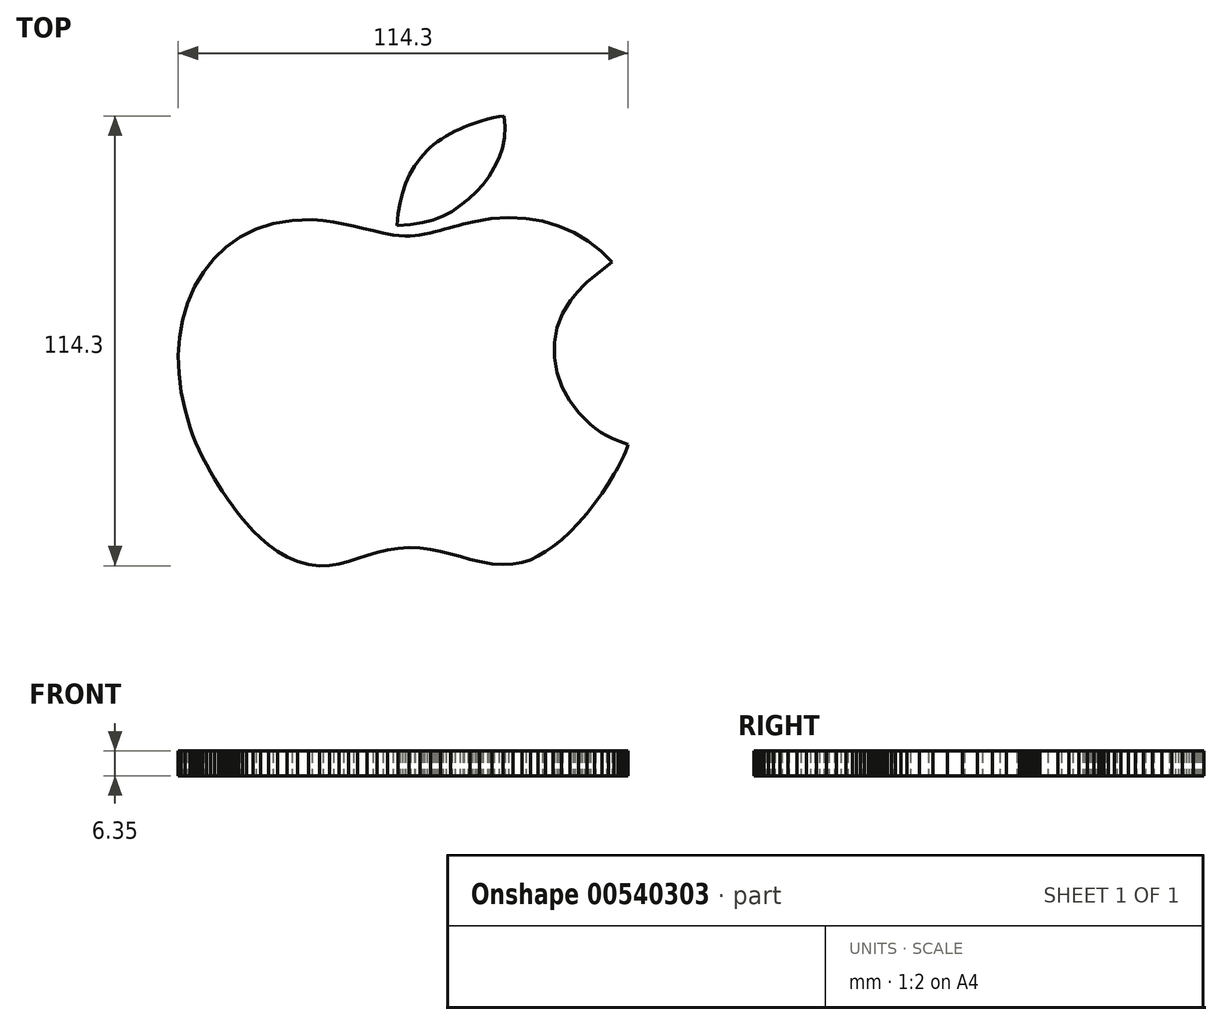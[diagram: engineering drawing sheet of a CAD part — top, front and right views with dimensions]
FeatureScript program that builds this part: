
annotation { "Feature Type Name" : "Feature", "Feature Type Description" : "" }
export const myFeature = defineFeature(function(context is Context, id is Id, definition is map)
    precondition{}
    {
        {
            var Q0;
            Q0=qCreatedBy(makeId("Top.planeOp"),FACE);
            var sketch = newSketch(context, id + "F0", { "sketchPlane" : qUnion([Q0])});
            skLineSegment(sketch, "E0", {"start": v(57.15, -26.3) * mm, "end": v(55.03, -25.53) * mm});
            skLineSegment(sketch, "E1", {"start": v(55.03, -25.53) * mm, "end": v(53.22, -24.8) * mm});
            skLineSegment(sketch, "E2", {"start": v(53.22, -24.8) * mm, "end": v(51.63, -24.04) * mm});
            skLineSegment(sketch, "E3", {"start": v(51.63, -24.04) * mm, "end": v(50.21, -23.21) * mm});
            skLineSegment(sketch, "E4", {"start": v(50.21, -23.21) * mm, "end": v(48.87, -22.28) * mm});
            skLineSegment(sketch, "E5", {"start": v(48.87, -22.28) * mm, "end": v(47.55, -21.17) * mm});
            skLineSegment(sketch, "E6", {"start": v(47.55, -21.17) * mm, "end": v(46.17, -19.86) * mm});
            skLineSegment(sketch, "E7", {"start": v(46.17, -19.86) * mm, "end": v(44.66, -18.29) * mm});
            skLineSegment(sketch, "E8", {"start": v(44.66, -18.29) * mm, "end": v(42.21, -15.16) * mm});
            skLineSegment(sketch, "E9", {"start": v(42.21, -15.16) * mm, "end": v(40.35, -11.72) * mm});
            skLineSegment(sketch, "E10", {"start": v(40.35, -11.72) * mm, "end": v(39.1, -8.04) * mm});
            skLineSegment(sketch, "E11", {"start": v(39.1, -8.04) * mm, "end": v(38.46, -4.24) * mm});
            skLineSegment(sketch, "E12", {"start": v(38.46, -4.24) * mm, "end": v(38.47, -0.4) * mm});
            skLineSegment(sketch, "E13", {"start": v(38.47, -0.4) * mm, "end": v(39.13, 3.35) * mm});
            skLineSegment(sketch, "E14", {"start": v(39.13, 3.35) * mm, "end": v(40.47, 6.94) * mm});
            skLineSegment(sketch, "E15", {"start": v(40.47, 6.94) * mm, "end": v(42.51, 10.25) * mm});
            skLineSegment(sketch, "E16", {"start": v(42.51, 10.25) * mm, "end": v(43.1, 11) * mm});
            skLineSegment(sketch, "E17", {"start": v(43.1, 11) * mm, "end": v(43.69, 11.73) * mm});
            skLineSegment(sketch, "E18", {"start": v(43.69, 11.73) * mm, "end": v(44.28, 12.42) * mm});
            skLineSegment(sketch, "E19", {"start": v(44.28, 12.42) * mm, "end": v(44.88, 13.08) * mm});
            skLineSegment(sketch, "E20", {"start": v(44.88, 13.08) * mm, "end": v(45.48, 13.71) * mm});
            skLineSegment(sketch, "E21", {"start": v(45.48, 13.71) * mm, "end": v(46.1, 14.33) * mm});
            skLineSegment(sketch, "E22", {"start": v(46.1, 14.33) * mm, "end": v(46.73, 14.92) * mm});
            skLineSegment(sketch, "E23", {"start": v(46.73, 14.92) * mm, "end": v(47.37, 15.49) * mm});
            skLineSegment(sketch, "E24", {"start": v(47.37, 15.49) * mm, "end": v(53.11, 20.04) * mm});
            skLineSegment(sketch, "E25", {"start": v(53.11, 20.04) * mm, "end": v(50.23, 22.83) * mm});
            skLineSegment(sketch, "E26", {"start": v(50.23, 22.83) * mm, "end": v(46.95, 25.43) * mm});
            skLineSegment(sketch, "E27", {"start": v(46.95, 25.43) * mm, "end": v(43.37, 27.57) * mm});
            skLineSegment(sketch, "E28", {"start": v(43.37, 27.57) * mm, "end": v(39.53, 29.23) * mm});
            skLineSegment(sketch, "E29", {"start": v(39.53, 29.23) * mm, "end": v(35.46, 30.42) * mm});
            skLineSegment(sketch, "E30", {"start": v(35.46, 30.42) * mm, "end": v(31.2, 31.12) * mm});
            skLineSegment(sketch, "E31", {"start": v(31.2, 31.12) * mm, "end": v(26.8, 31.33) * mm});
            skLineSegment(sketch, "E32", {"start": v(26.8, 31.33) * mm, "end": v(22.27, 31.05) * mm});
            skLineSegment(sketch, "E33", {"start": v(22.27, 31.05) * mm, "end": v(17.67, 30.26) * mm});
            skLineSegment(sketch, "E34", {"start": v(17.67, 30.26) * mm, "end": v(16.45, 29.98) * mm});
            skLineSegment(sketch, "E35", {"start": v(16.45, 29.98) * mm, "end": v(15.24, 29.67) * mm});
            skLineSegment(sketch, "E36", {"start": v(15.24, 29.67) * mm, "end": v(14.06, 29.36) * mm});
            skLineSegment(sketch, "E37", {"start": v(14.06, 29.36) * mm, "end": v(12.88, 29.03) * mm});
            skLineSegment(sketch, "E38", {"start": v(12.88, 29.03) * mm, "end": v(11.71, 28.7) * mm});
            skLineSegment(sketch, "E39", {"start": v(11.71, 28.7) * mm, "end": v(10.54, 28.38) * mm});
            skLineSegment(sketch, "E40", {"start": v(10.54, 28.38) * mm, "end": v(9.36, 28.07) * mm});
            skLineSegment(sketch, "E41", {"start": v(9.36, 28.07) * mm, "end": v(8.17, 27.77) * mm});
            skLineSegment(sketch, "E42", {"start": v(8.17, 27.77) * mm, "end": v(6.77, 27.44) * mm});
            skLineSegment(sketch, "E43", {"start": v(6.77, 27.44) * mm, "end": v(5.47, 27.15) * mm});
            skLineSegment(sketch, "E44", {"start": v(5.47, 27.15) * mm, "end": v(4.22, 26.9) * mm});
            skLineSegment(sketch, "E45", {"start": v(4.22, 26.9) * mm, "end": v(3, 26.74) * mm});
            skLineSegment(sketch, "E46", {"start": v(3, 26.74) * mm, "end": v(1.74, 26.64) * mm});
            skLineSegment(sketch, "E47", {"start": v(1.74, 26.64) * mm, "end": v(0.42, 26.64) * mm});
            skLineSegment(sketch, "E48", {"start": v(0.42, 26.64) * mm, "end": v(-1, 26.74) * mm});
            skLineSegment(sketch, "E49", {"start": v(-1, 26.74) * mm, "end": v(-2.54, 26.95) * mm});
            skLineSegment(sketch, "E50", {"start": v(-2.54, 26.95) * mm, "end": v(-5.12, 27.44) * mm});
            skLineSegment(sketch, "E51", {"start": v(-5.12, 27.44) * mm, "end": v(-7.63, 28) * mm});
            skLineSegment(sketch, "E52", {"start": v(-7.63, 28) * mm, "end": v(-10.1, 28.6) * mm});
            skLineSegment(sketch, "E53", {"start": v(-10.1, 28.6) * mm, "end": v(-12.59, 29.19) * mm});
            skLineSegment(sketch, "E54", {"start": v(-12.59, 29.19) * mm, "end": v(-15.1, 29.74) * mm});
            skLineSegment(sketch, "E55", {"start": v(-15.1, 29.74) * mm, "end": v(-17.66, 30.21) * mm});
            skLineSegment(sketch, "E56", {"start": v(-17.66, 30.21) * mm, "end": v(-20.32, 30.57) * mm});
            skLineSegment(sketch, "E57", {"start": v(-20.32, 30.57) * mm, "end": v(-23.1, 30.78) * mm});
            skLineSegment(sketch, "E58", {"start": v(-23.1, 30.78) * mm, "end": v(-28.26, 30.65) * mm});
            skLineSegment(sketch, "E59", {"start": v(-28.26, 30.65) * mm, "end": v(-33.04, 29.83) * mm});
            skLineSegment(sketch, "E60", {"start": v(-33.04, 29.83) * mm, "end": v(-37.42, 28.39) * mm});
            skLineSegment(sketch, "E61", {"start": v(-37.42, 28.39) * mm, "end": v(-41.4, 26.38) * mm});
            skLineSegment(sketch, "E62", {"start": v(-41.4, 26.38) * mm, "end": v(-44.95, 23.86) * mm});
            skLineSegment(sketch, "E63", {"start": v(-44.95, 23.86) * mm, "end": v(-48.07, 20.9) * mm});
            skLineSegment(sketch, "E64", {"start": v(-48.07, 20.9) * mm, "end": v(-50.74, 17.55) * mm});
            skLineSegment(sketch, "E65", {"start": v(-50.74, 17.55) * mm, "end": v(-52.97, 13.87) * mm});
            skLineSegment(sketch, "E66", {"start": v(-52.97, 13.87) * mm, "end": v(-54.81, 9.68) * mm});
            skLineSegment(sketch, "E67", {"start": v(-54.81, 9.68) * mm, "end": v(-56.1, 5.33) * mm});
            skLineSegment(sketch, "E68", {"start": v(-56.1, 5.33) * mm, "end": v(-56.87, 0.85) * mm});
            skLineSegment(sketch, "E69", {"start": v(-56.87, 0.85) * mm, "end": v(-57.15, -3.71) * mm});
            skLineSegment(sketch, "E70", {"start": v(-57.15, -3.71) * mm, "end": v(-56.98, -8.31) * mm});
            skLineSegment(sketch, "E71", {"start": v(-56.98, -8.31) * mm, "end": v(-56.4, -12.91) * mm});
            skLineSegment(sketch, "E72", {"start": v(-56.4, -12.91) * mm, "end": v(-55.44, -17.47) * mm});
            skLineSegment(sketch, "E73", {"start": v(-55.44, -17.47) * mm, "end": v(-54.13, -21.94) * mm});
            skLineSegment(sketch, "E74", {"start": v(-54.13, -21.94) * mm, "end": v(-53.44, -23.86) * mm});
            skLineSegment(sketch, "E75", {"start": v(-53.44, -23.86) * mm, "end": v(-52.68, -25.78) * mm});
            skLineSegment(sketch, "E76", {"start": v(-52.68, -25.78) * mm, "end": v(-51.83, -27.7) * mm});
            skLineSegment(sketch, "E77", {"start": v(-51.83, -27.7) * mm, "end": v(-50.93, -29.58) * mm});
            skLineSegment(sketch, "E78", {"start": v(-50.93, -29.58) * mm, "end": v(-49.97, -31.45) * mm});
            skLineSegment(sketch, "E79", {"start": v(-49.97, -31.45) * mm, "end": v(-48.96, -33.27) * mm});
            skLineSegment(sketch, "E80", {"start": v(-48.96, -33.27) * mm, "end": v(-47.92, -35.03) * mm});
            skLineSegment(sketch, "E81", {"start": v(-47.92, -35.03) * mm, "end": v(-46.86, -36.73) * mm});
            skLineSegment(sketch, "E82", {"start": v(-46.86, -36.73) * mm, "end": v(-45.99, -38.08) * mm});
            skLineSegment(sketch, "E83", {"start": v(-45.99, -38.08) * mm, "end": v(-45.15, -39.34) * mm});
            skLineSegment(sketch, "E84", {"start": v(-45.15, -39.34) * mm, "end": v(-44.33, -40.55) * mm});
            skLineSegment(sketch, "E85", {"start": v(-44.33, -40.55) * mm, "end": v(-43.5, -41.7) * mm});
            skLineSegment(sketch, "E86", {"start": v(-43.5, -41.7) * mm, "end": v(-42.66, -42.85) * mm});
            skLineSegment(sketch, "E87", {"start": v(-42.66, -42.85) * mm, "end": v(-41.77, -44) * mm});
            skLineSegment(sketch, "E88", {"start": v(-41.77, -44) * mm, "end": v(-40.82, -45.18) * mm});
            skLineSegment(sketch, "E89", {"start": v(-40.82, -45.18) * mm, "end": v(-39.8, -46.4) * mm});
            skLineSegment(sketch, "E90", {"start": v(-39.8, -46.4) * mm, "end": v(-38.12, -48.26) * mm});
            skLineSegment(sketch, "E91", {"start": v(-38.12, -48.26) * mm, "end": v(-36.24, -50.1) * mm});
            skLineSegment(sketch, "E92", {"start": v(-36.24, -50.1) * mm, "end": v(-34.16, -51.88) * mm});
            skLineSegment(sketch, "E93", {"start": v(-34.16, -51.88) * mm, "end": v(-31.89, -53.52) * mm});
            skLineSegment(sketch, "E94", {"start": v(-31.89, -53.52) * mm, "end": v(-29.45, -54.93) * mm});
            skLineSegment(sketch, "E95", {"start": v(-29.45, -54.93) * mm, "end": v(-26.84, -56.06) * mm});
            skLineSegment(sketch, "E96", {"start": v(-26.84, -56.06) * mm, "end": v(-24.1, -56.82) * mm});
            skLineSegment(sketch, "E97", {"start": v(-24.1, -56.82) * mm, "end": v(-21.2, -57.15) * mm});
            skLineSegment(sketch, "E98", {"start": v(-21.2, -57.15) * mm, "end": v(-18.73, -57.05) * mm});
            skLineSegment(sketch, "E99", {"start": v(-18.73, -57.05) * mm, "end": v(-16.32, -56.65) * mm});
            skLineSegment(sketch, "E100", {"start": v(-16.32, -56.65) * mm, "end": v(-13.93, -56.05) * mm});
            skLineSegment(sketch, "E101", {"start": v(-13.93, -56.05) * mm, "end": v(-11.54, -55.32) * mm});
            skLineSegment(sketch, "E102", {"start": v(-11.54, -55.32) * mm, "end": v(-9.12, -54.54) * mm});
            skLineSegment(sketch, "E103", {"start": v(-9.12, -54.54) * mm, "end": v(-6.62, -53.78) * mm});
            skLineSegment(sketch, "E104", {"start": v(-6.62, -53.78) * mm, "end": v(-4.01, -53.13) * mm});
            skLineSegment(sketch, "E105", {"start": v(-4.01, -53.13) * mm, "end": v(-1.27, -52.67) * mm});
            skLineSegment(sketch, "E106", {"start": v(-1.27, -52.67) * mm, "end": v(1.54, -52.5) * mm});
            skLineSegment(sketch, "E107", {"start": v(1.54, -52.5) * mm, "end": v(4.27, -52.61) * mm});
            skLineSegment(sketch, "E108", {"start": v(4.27, -52.61) * mm, "end": v(6.93, -52.96) * mm});
            skLineSegment(sketch, "E109", {"start": v(6.93, -52.96) * mm, "end": v(9.52, -53.48) * mm});
            skLineSegment(sketch, "E110", {"start": v(9.52, -53.48) * mm, "end": v(12.06, -54.1) * mm});
            skLineSegment(sketch, "E111", {"start": v(12.06, -54.1) * mm, "end": v(14.55, -54.79) * mm});
            skLineSegment(sketch, "E112", {"start": v(14.55, -54.79) * mm, "end": v(17, -55.46) * mm});
            skLineSegment(sketch, "E113", {"start": v(17, -55.46) * mm, "end": v(19.4, -56.06) * mm});
            skLineSegment(sketch, "E114", {"start": v(19.4, -56.06) * mm, "end": v(22.57, -56.62) * mm});
            skLineSegment(sketch, "E115", {"start": v(22.57, -56.62) * mm, "end": v(25.4, -56.83) * mm});
            skLineSegment(sketch, "E116", {"start": v(25.4, -56.83) * mm, "end": v(27.92, -56.7) * mm});
            skLineSegment(sketch, "E117", {"start": v(27.92, -56.7) * mm, "end": v(30.21, -56.28) * mm});
            skLineSegment(sketch, "E118", {"start": v(30.21, -56.28) * mm, "end": v(32.32, -55.59) * mm});
            skLineSegment(sketch, "E119", {"start": v(32.32, -55.59) * mm, "end": v(34.3, -54.66) * mm});
            skLineSegment(sketch, "E120", {"start": v(34.3, -54.66) * mm, "end": v(36.22, -53.54) * mm});
            skLineSegment(sketch, "E121", {"start": v(36.22, -53.54) * mm, "end": v(38.12, -52.26) * mm});
            skLineSegment(sketch, "E122", {"start": v(38.12, -52.26) * mm, "end": v(40.27, -50.56) * mm});
            skLineSegment(sketch, "E123", {"start": v(40.27, -50.56) * mm, "end": v(42.44, -48.55) * mm});
            skLineSegment(sketch, "E124", {"start": v(42.44, -48.55) * mm, "end": v(44.58, -46.29) * mm});
            skLineSegment(sketch, "E125", {"start": v(44.58, -46.29) * mm, "end": v(46.67, -43.86) * mm});
            skLineSegment(sketch, "E126", {"start": v(46.67, -43.86) * mm, "end": v(48.65, -41.33) * mm});
            skLineSegment(sketch, "E127", {"start": v(48.65, -41.33) * mm, "end": v(50.5, -38.77) * mm});
            skLineSegment(sketch, "E128", {"start": v(50.5, -38.77) * mm, "end": v(52.15, -36.25) * mm});
            skLineSegment(sketch, "E129", {"start": v(52.15, -36.25) * mm, "end": v(53.58, -33.85) * mm});
            skLineSegment(sketch, "E130", {"start": v(53.58, -33.85) * mm, "end": v(54.04, -33.03) * mm});
            skLineSegment(sketch, "E131", {"start": v(54.04, -33.03) * mm, "end": v(54.53, -32.13) * mm});
            skLineSegment(sketch, "E132", {"start": v(54.53, -32.13) * mm, "end": v(55.05, -31.17) * mm});
            skLineSegment(sketch, "E133", {"start": v(55.05, -31.17) * mm, "end": v(55.56, -30.16) * mm});
            skLineSegment(sketch, "E134", {"start": v(55.56, -30.16) * mm, "end": v(56.05, -29.15) * mm});
            skLineSegment(sketch, "E135", {"start": v(56.05, -29.15) * mm, "end": v(56.5, -28.15) * mm});
            skLineSegment(sketch, "E136", {"start": v(56.5, -28.15) * mm, "end": v(56.86, -27.2) * mm});
            skLineSegment(sketch, "E137", {"start": v(56.86, -27.2) * mm, "end": v(57.15, -26.3) * mm});
            skLineSegment(sketch, "E138", {"start": v(-1.54, 29.38) * mm, "end": v(1.88, 29.59) * mm});
            skLineSegment(sketch, "E139", {"start": v(1.88, 29.59) * mm, "end": v(4.92, 30.04) * mm});
            skLineSegment(sketch, "E140", {"start": v(4.92, 30.04) * mm, "end": v(7.63, 30.74) * mm});
            skLineSegment(sketch, "E141", {"start": v(7.63, 30.74) * mm, "end": v(10.09, 31.7) * mm});
            skLineSegment(sketch, "E142", {"start": v(10.09, 31.7) * mm, "end": v(12.36, 32.9) * mm});
            skLineSegment(sketch, "E143", {"start": v(12.36, 32.9) * mm, "end": v(14.5, 34.35) * mm});
            skLineSegment(sketch, "E144", {"start": v(14.5, 34.35) * mm, "end": v(16.58, 36.05) * mm});
            skLineSegment(sketch, "E145", {"start": v(16.58, 36.05) * mm, "end": v(18.67, 38.01) * mm});
            skLineSegment(sketch, "E146", {"start": v(18.67, 38.01) * mm, "end": v(20.25, 39.74) * mm});
            skLineSegment(sketch, "E147", {"start": v(20.25, 39.74) * mm, "end": v(21.76, 41.75) * mm});
            skLineSegment(sketch, "E148", {"start": v(21.76, 41.75) * mm, "end": v(23.14, 44) * mm});
            skLineSegment(sketch, "E149", {"start": v(23.14, 44) * mm, "end": v(24.32, 46.44) * mm});
            skLineSegment(sketch, "E150", {"start": v(24.32, 46.44) * mm, "end": v(25.21, 49.03) * mm});
            skLineSegment(sketch, "E151", {"start": v(25.21, 49.03) * mm, "end": v(25.77, 51.7) * mm});
            skLineSegment(sketch, "E152", {"start": v(25.77, 51.7) * mm, "end": v(25.9, 54.43) * mm});
            skLineSegment(sketch, "E153", {"start": v(25.9, 54.43) * mm, "end": v(25.56, 57.15) * mm});
            skLineSegment(sketch, "E154", {"start": v(25.56, 57.15) * mm, "end": v(24.35, 57.01) * mm});
            skLineSegment(sketch, "E155", {"start": v(24.35, 57.01) * mm, "end": v(22.93, 56.72) * mm});
            skLineSegment(sketch, "E156", {"start": v(22.93, 56.72) * mm, "end": v(21.37, 56.32) * mm});
            skLineSegment(sketch, "E157", {"start": v(21.37, 56.32) * mm, "end": v(19.77, 55.83) * mm});
            skLineSegment(sketch, "E158", {"start": v(19.77, 55.83) * mm, "end": v(18.2, 55.31) * mm});
            skLineSegment(sketch, "E159", {"start": v(18.2, 55.31) * mm, "end": v(16.73, 54.79) * mm});
            skLineSegment(sketch, "E160", {"start": v(16.73, 54.79) * mm, "end": v(15.46, 54.3) * mm});
            skLineSegment(sketch, "E161", {"start": v(15.46, 54.3) * mm, "end": v(14.46, 53.9) * mm});
            skLineSegment(sketch, "E162", {"start": v(14.46, 53.9) * mm, "end": v(13.2, 53.31) * mm});
            skLineSegment(sketch, "E163", {"start": v(13.2, 53.31) * mm, "end": v(12, 52.69) * mm});
            skLineSegment(sketch, "E164", {"start": v(12, 52.69) * mm, "end": v(10.84, 52.02) * mm});
            skLineSegment(sketch, "E165", {"start": v(10.84, 52.02) * mm, "end": v(9.75, 51.32) * mm});
            skLineSegment(sketch, "E166", {"start": v(9.75, 51.32) * mm, "end": v(8.72, 50.6) * mm});
            skLineSegment(sketch, "E167", {"start": v(8.72, 50.6) * mm, "end": v(7.76, 49.85) * mm});
            skLineSegment(sketch, "E168", {"start": v(7.76, 49.85) * mm, "end": v(6.87, 49.09) * mm});
            skLineSegment(sketch, "E169", {"start": v(6.87, 49.09) * mm, "end": v(6.07, 48.31) * mm});
            skLineSegment(sketch, "E170", {"start": v(6.07, 48.31) * mm, "end": v(4.37, 46.42) * mm});
            skLineSegment(sketch, "E171", {"start": v(4.37, 46.42) * mm, "end": v(2.9, 44.42) * mm});
            skLineSegment(sketch, "E172", {"start": v(2.9, 44.42) * mm, "end": v(1.65, 42.3) * mm});
            skLineSegment(sketch, "E173", {"start": v(1.65, 42.3) * mm, "end": v(0.62, 40.04) * mm});
            skLineSegment(sketch, "E174", {"start": v(0.62, 40.04) * mm, "end": v(-0.21, 37.63) * mm});
            skLineSegment(sketch, "E175", {"start": v(-0.21, 37.63) * mm, "end": v(-0.84, 35.06) * mm});
            skLineSegment(sketch, "E176", {"start": v(-0.84, 35.06) * mm, "end": v(-1.28, 32.31) * mm});
            skLineSegment(sketch, "E177", {"start": v(-1.28, 32.31) * mm, "end": v(-1.54, 29.38) * mm});
            skSolve(sketch);
        }
        {
            var Q0;
            Q0=makeQuery(id+"F0.imprint","IMPRINT",FACE,{"disambiguationData":[TD([[makeQuery(id+"F0.imprint","IMPRINT",EDGE,{"derivedFrom":sQuery(id+"F0.wireOp",EDGE,"E0")}),1.0]])]});
            extrude(context, id + "F1", {"entities" : qUnion([Q0]), "depth" : 6.35 * mm, "offsetDistance" : 25.4 * mm});
        }
        {
            var Q0;
            Q0=makeQuery(id+"F0.imprint","IMPRINT",FACE,{"disambiguationData":[TD([[makeQuery(id+"F0.imprint","IMPRINT",EDGE,{"derivedFrom":sQuery(id+"F0.wireOp",EDGE,"E138")}),1.0]])]});
            extrude(context, id + "F2", {"entities" : qUnion([Q0]), "depth" : 6.35 * mm, "offsetDistance" : 25.4 * mm});
        }
    });
